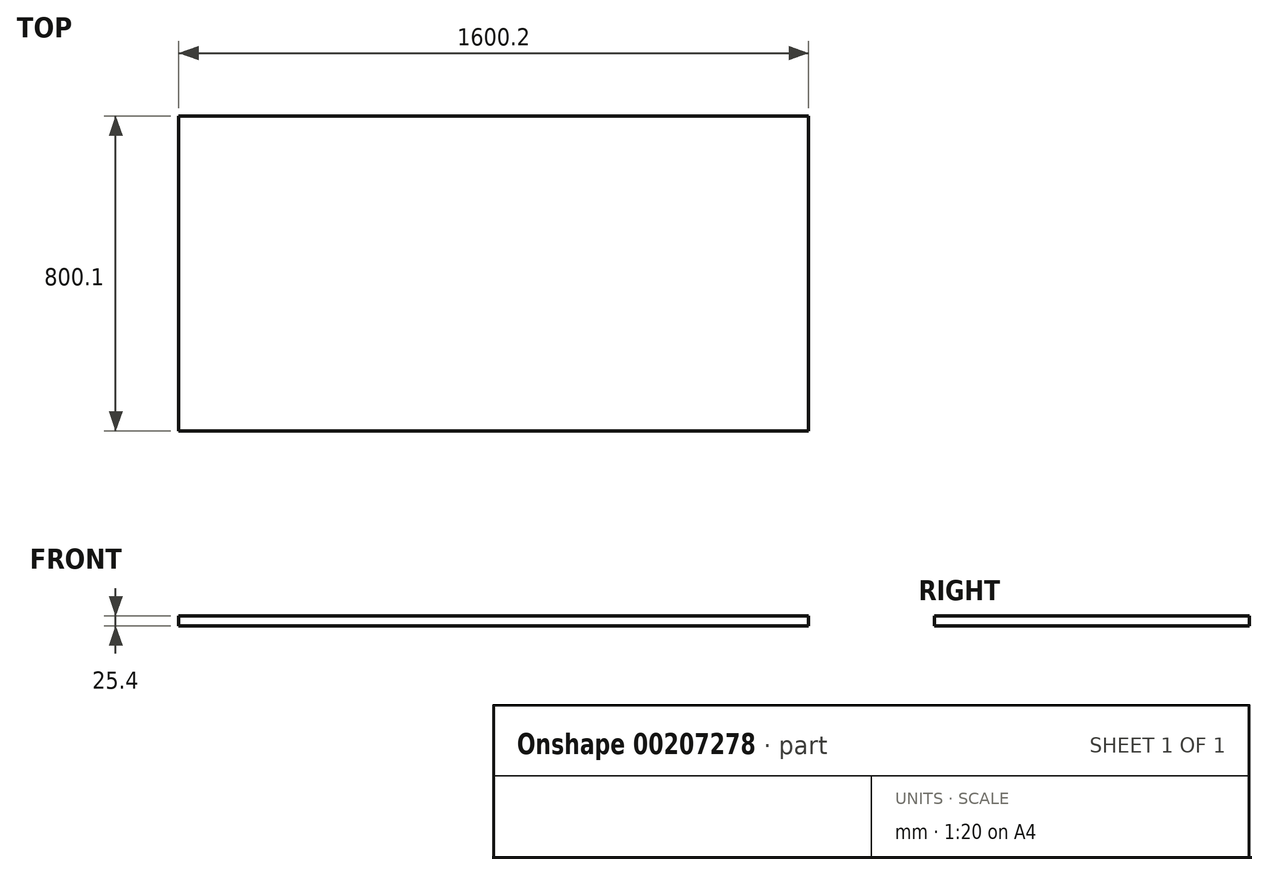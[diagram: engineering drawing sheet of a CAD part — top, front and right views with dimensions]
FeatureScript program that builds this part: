
annotation { "Feature Type Name" : "Feature", "Feature Type Description" : "" }
export const myFeature = defineFeature(function(context is Context, id is Id, definition is map)
    precondition{}
    {
        {
            var Q0;
            Q0=qCreatedBy(makeId("Top.planeOp"),FACE);
            var sketch = newSketch(context, id + "F0", { "sketchPlane" : qUnion([Q0])});
            skLineSegment(sketch, "E0.bottom", {"start": v(-800.1, -400.05) * mm, "end": v(800.1, -400.05) * mm});
            skLineSegment(sketch, "E0.top", {"start": v(-800.1, 400.05) * mm, "end": v(800.1, 400.05) * mm});
            skLineSegment(sketch, "E0.left", {"start": v(-800.1, -400.05) * mm, "end": v(-800.1, 400.05) * mm});
            skLineSegment(sketch, "E0.right", {"start": v(800.1, -400.05) * mm, "end": v(800.1, 400.05) * mm});
            skPoint(sketch, "E0.middle", {"position": v(0, 0) * mm});
            skSolve(sketch);
        }
        {
            var Q0;
            Q0=makeQuery(id+"F0.imprint","IMPRINT",FACE,{"disambiguationData":[TD([[makeQuery(id+"F0.imprint","IMPRINT",EDGE,{"derivedFrom":sQuery(id+"F0.wireOp",EDGE,"E0.bottom")}),1.0]])]});
            extrude(context, id + "F1", {"entities" : qUnion([Q0]), "depth" : 25.4 * mm});
        }
    });
